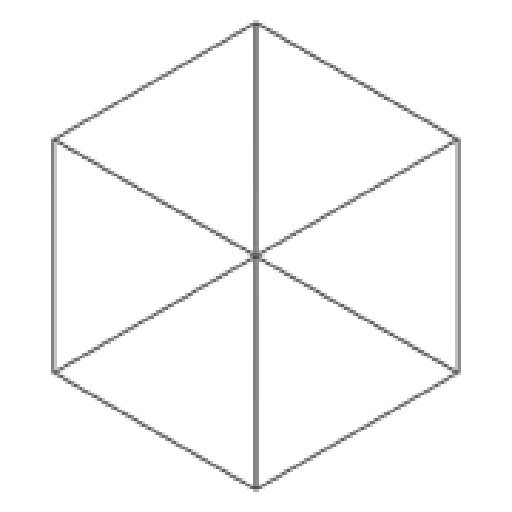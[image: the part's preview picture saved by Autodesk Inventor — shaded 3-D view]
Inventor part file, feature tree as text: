
AUTODESK INVENTOR PART (.ipt)
format: ipt  version: 2023 (Build 270158000, 158)  size: 194,560 bytes
history: native  units: in
note: dims shown in document units (in); Inventor stores cm internally (conversion verified against a paired STEP export)
features: extrude x4, sketch x4, projected_geometry x3, fillet x1
ambient origin geometry x8: Origin, YZ Plane, XZ Plane, XY Plane, X Axis, Y Axis, Z Axis, Center Point
bodies: Solid1 (feature_tree)
feature tree (12):
  extrude  "Extrusion1"  Depth=108.2677in TaperAngle=0.0deg
  extrude  "Extrusion2"  TaperAngle=0.0deg  [1 undecoded]
  extrude  "Extrusion3"  TaperAngle=0.0deg  [1 undecoded]
  extrude  "Extrusion4"  TaperAngle=0.0deg  [1 undecoded]
  fillet  "Fillet1"  Radius=0.25in
  sketch  "Sketch1"  dims[d0=108.2677in d2=108.2677in d3=0.0in]
  sketch  "Sketch2"  dims[d4=1.0in d5=0.0in d6=0.0in]
  projected_geometry  "Projected Loop1"
  sketch  "Sketch3"  dims[d7=1.0in d8=0.0in d9=0.0in]
  projected_geometry  "Projected Loop2"
  sketch  "Sketch4"  dims[d10=1.0in d11=0.0in d12=0.0in d13=0.25in]
  projected_geometry  "Projected Loop3"
note: 3 required parameter values undecoded (feature->parameter linkage not recoverable at this tier; creation-order binding heuristic only, values carry confidence <= 0.55)
